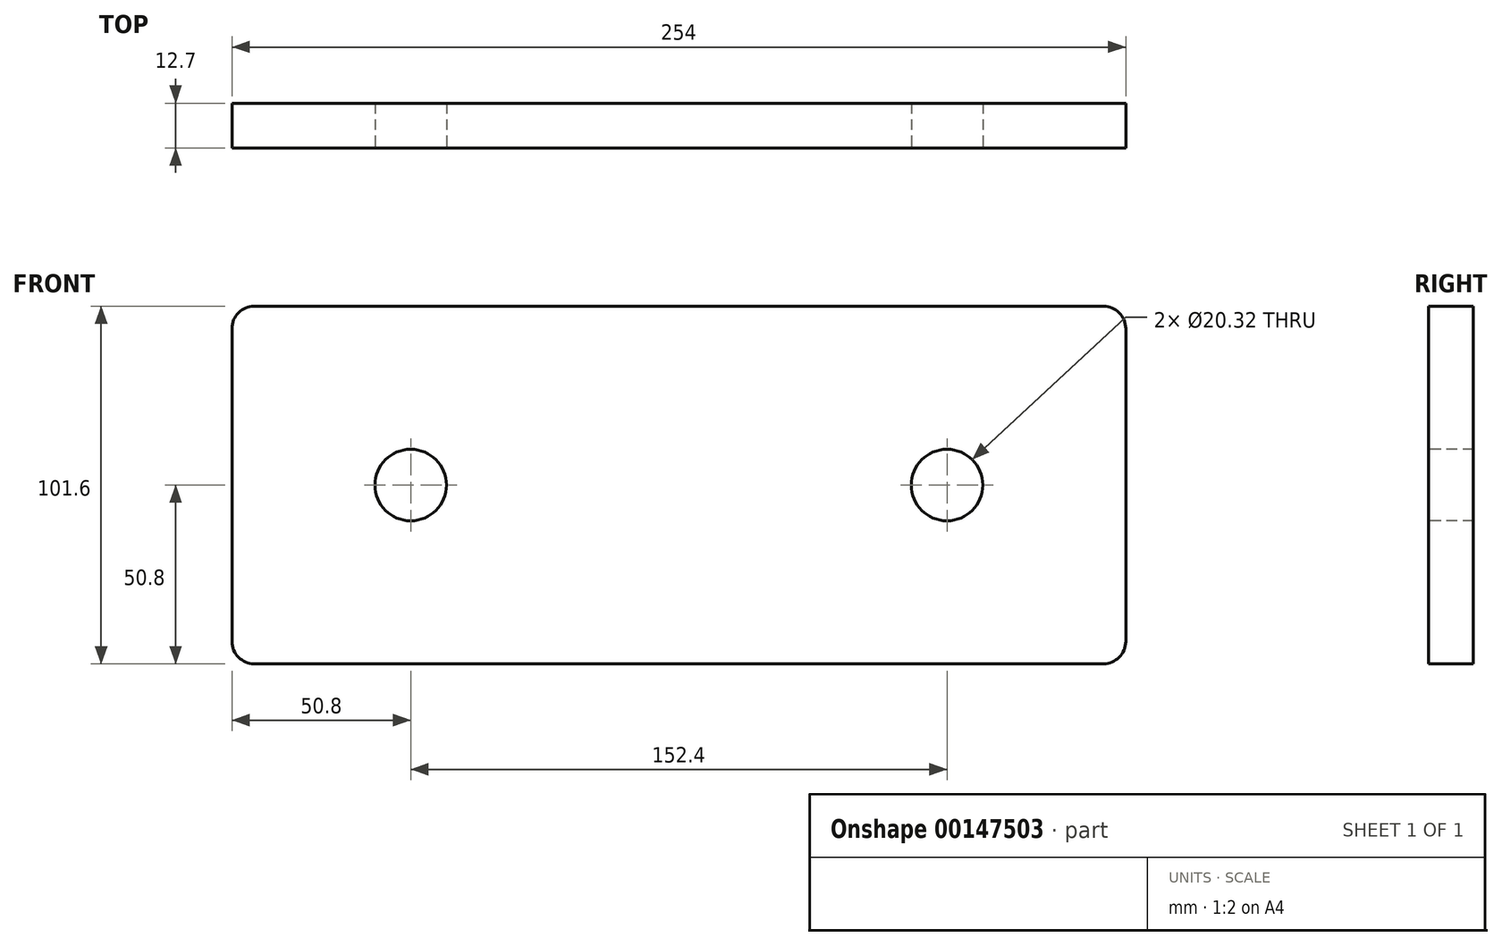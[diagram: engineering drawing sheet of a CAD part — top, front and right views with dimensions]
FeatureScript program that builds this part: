
annotation { "Feature Type Name" : "Feature", "Feature Type Description" : "" }
export const myFeature = defineFeature(function(context is Context, id is Id, definition is map)
    precondition{}
    {
        {
            var Q0;
            Q0=qCreatedBy(makeId("Front.planeOp"),FACE);
            var sketch = newSketch(context, id + "F0", { "sketchPlane" : qUnion([Q0])});
            skLineSegment(sketch, "E0.bottom", {"start": v(0, 0) * mm, "end": v(254, 0) * mm});
            skLineSegment(sketch, "E0.top", {"start": v(0, 101.6) * mm, "end": v(254, 101.6) * mm});
            skLineSegment(sketch, "E0.left", {"start": v(0, 0) * mm, "end": v(0, 101.6) * mm});
            skLineSegment(sketch, "E0.right", {"start": v(254, 0) * mm, "end": v(254, 101.6) * mm});
            skSolve(sketch);
        }
        {
            var Q0;
            Q0 = qSketchRegion(id + "F0", true);
            extrude(context, id + "F1", {"entities" : qUnion([Q0]), "depth" : 12.7 * mm});
        }
        {
            var Q0;
            Q0=makeQuery(id+"F1.opExtrude","CAP_FACE",FACE,{"disambiguationData":[OSD([sQuery(id+"F0.wireOp",EDGE,"E0.bottom"),sQuery(id+"F0.wireOp",EDGE,"E0.top"),sQuery(id+"F0.wireOp",EDGE,"E0.left"),sQuery(id+"F0.wireOp",EDGE,"E0.right")])],"isStart":false});
            var sketch = newSketch(context, id + "F2", { "sketchPlane" : qUnion([Q0])});
            skCircle(sketch, "E1", {"center": v(50.8, 50.8) * mm, "radius": 10.16 * mm});
            skPoint(sketch, "E1.centerSnap0", {"position": v(0, 50.8) * mm});
            skCircle(sketch, "E2", {"center": v(203.2, 50.8) * mm, "radius": 10.16 * mm});
            skSolve(sketch);
        }
        {
            var Q0;
            Q0 = qSketchRegion(id + "F2", true);
            extrude(context, id + "F3", {"entities" : qUnion([Q0]), "operationType" : NewBodyOperationType.REMOVE, "oppositeDirection" : true, "depth" : 25.4 * mm});
        }
        {
            var Q0;
            Q0=makeQuery(id+"F1.opExtrude","SWEPT_EDGE",EDGE,{"disambiguationData":[OSD([sQuery(id+"F0.wireOp",EDGE,"E0.top"),sQuery(id+"F0.wireOp",EDGE,"E0.left")])]});
            var Q1;
            Q1=makeQuery(id+"F1.opExtrude","SWEPT_EDGE",EDGE,{"disambiguationData":[OSD([sQuery(id+"F0.wireOp",EDGE,"E0.top"),sQuery(id+"F0.wireOp",EDGE,"E0.right")])]});
            var Q2;
            Q2=makeQuery(id+"F1.opExtrude","SWEPT_EDGE",EDGE,{"disambiguationData":[OSD([sQuery(id+"F0.wireOp",EDGE,"E0.bottom"),sQuery(id+"F0.wireOp",EDGE,"E0.right")])]});
            var Q3;
            Q3=makeQuery(id+"F1.opExtrude","SWEPT_EDGE",EDGE,{"disambiguationData":[OSD([sQuery(id+"F0.wireOp",EDGE,"E0.bottom"),sQuery(id+"F0.wireOp",EDGE,"E0.left")])]});
            fillet(context, id + "F4", {"entities" : qUnion([Q0, Q1, Q2, Q3]), "radius" : 6.35 * mm, "tangentPropagation" : true, "allowEdgeOverflow" : false});
        }
    });
